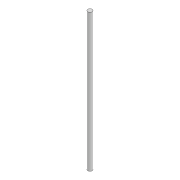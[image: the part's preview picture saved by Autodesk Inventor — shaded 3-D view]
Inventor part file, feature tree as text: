
AUTODESK INVENTOR PART (.ipt)
format: ipt  version: 2022 (Build 260153000, 153)  size: 73,728 bytes
history: native  units: mm
features: extrude x1, sketch x1
ambient origin geometry x8: Origin, YZ Plane, XZ Plane, XY Plane, X Axis, Y Axis, Z Axis, Center Point
bodies: Solid1 (feature_tree)
feature tree (2):
  extrude  "Extrusion1"  Depth=150.0mm TaperAngle=0.0deg
  sketch  "Sketch1"  dims[d0=4.8mm d1=150.0mm d2=0.0mm]
